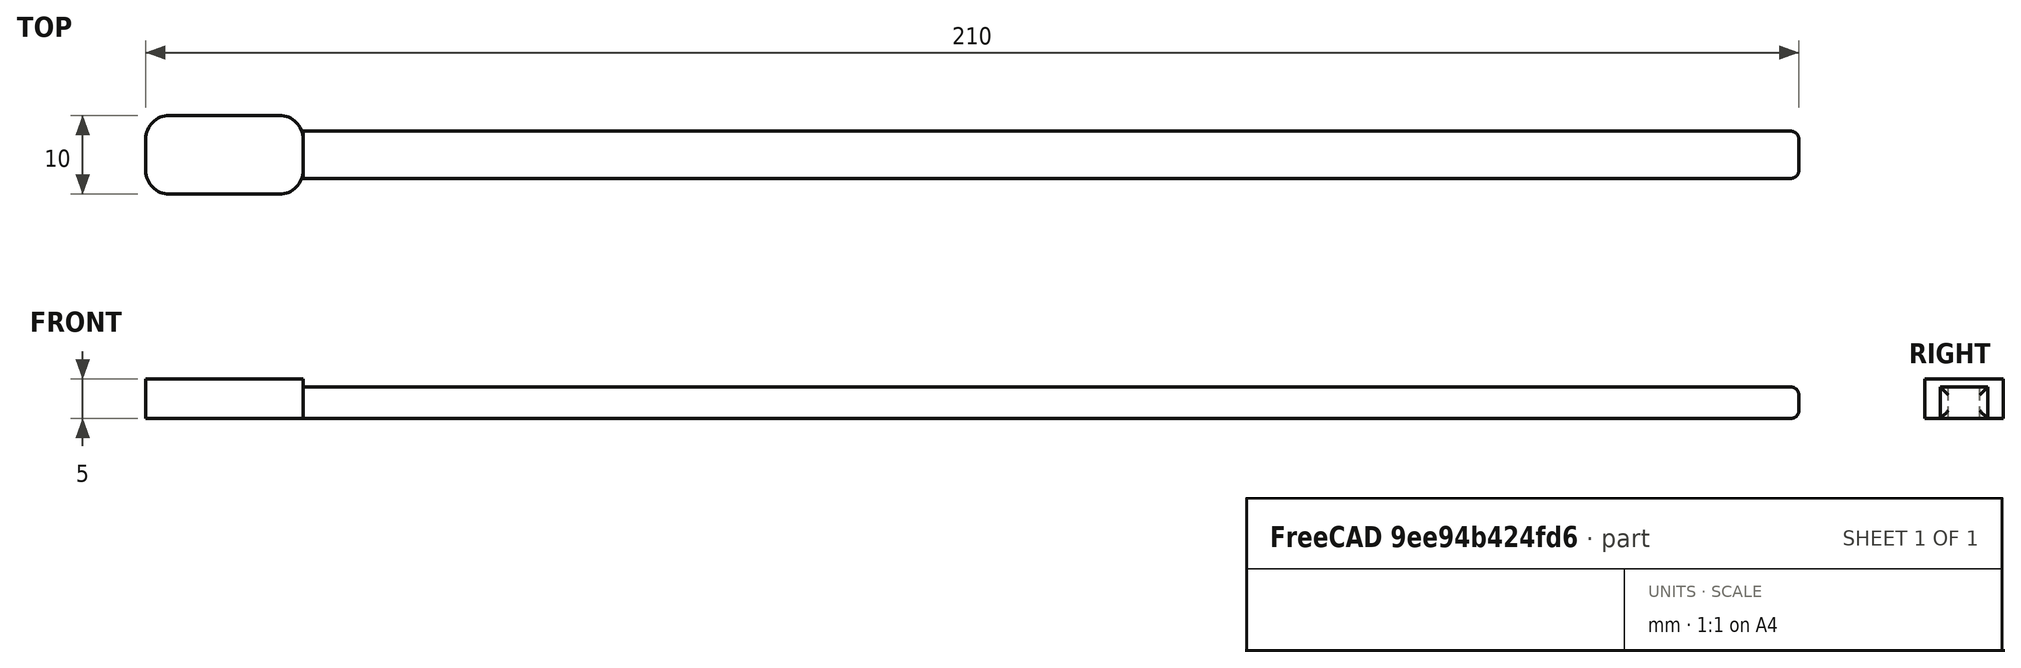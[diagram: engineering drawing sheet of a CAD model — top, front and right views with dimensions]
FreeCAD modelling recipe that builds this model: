
FCSTD DOCUMENT  (FreeCAD 0.20R29410 (Git))
Label: spade
License: All rights reserved
LicenseURL: http://en.wikipedia.org/wiki/All_rights_reserved
objects: Part::Box×2, Part::Fillet×2, Part::MultiFuse×1
note: 5 computed .brp shape members not serialized (recipe doc carries the construction recipe); baked Part::Feature solids carry a one-line shape summary decoded from their .brp

FEATURE [Part::Box] Box  label="handle"
  AttacherType = Attacher::AttachEngine3D
  Height = 4
  Length = 190
  Placement = pos=(0,-3,0) rot=(0,0,1;0rad)
  Width = 6
  expr: .Placement.Base.y = -Width / 2
FEATURE [Part::Box] Box001  label="scoop"
  AttacherType = Attacher::AttachEngine3D
  Height = 5
  Length = 20
  Placement = pos=(-20,-5,0) rot=(0,0,1;0rad)
  Width = 10
  expr: .Placement.Base.x = -Length
  expr: .Placement.Base.y = -Width / 2
  expr: Height = <<handle>>.Height + 1mm
FEATURE [Part::Fillet] Fillet  label="scoop fillet"
  Base = -> Box001
  Edges = 4 edges r=3: [Edge1,Edge3,Edge5,Edge7]
FEATURE [Part::Fillet] Fillet001  label="handle fillet"
  Base = -> Box
  Edges = 4 edges r=1: [Edge5,Edge6,Edge7,Edge8]
FEATURE [Part::MultiFuse] Fusion  label="spade"
  Shapes = -> [Fillet,Fillet001]
